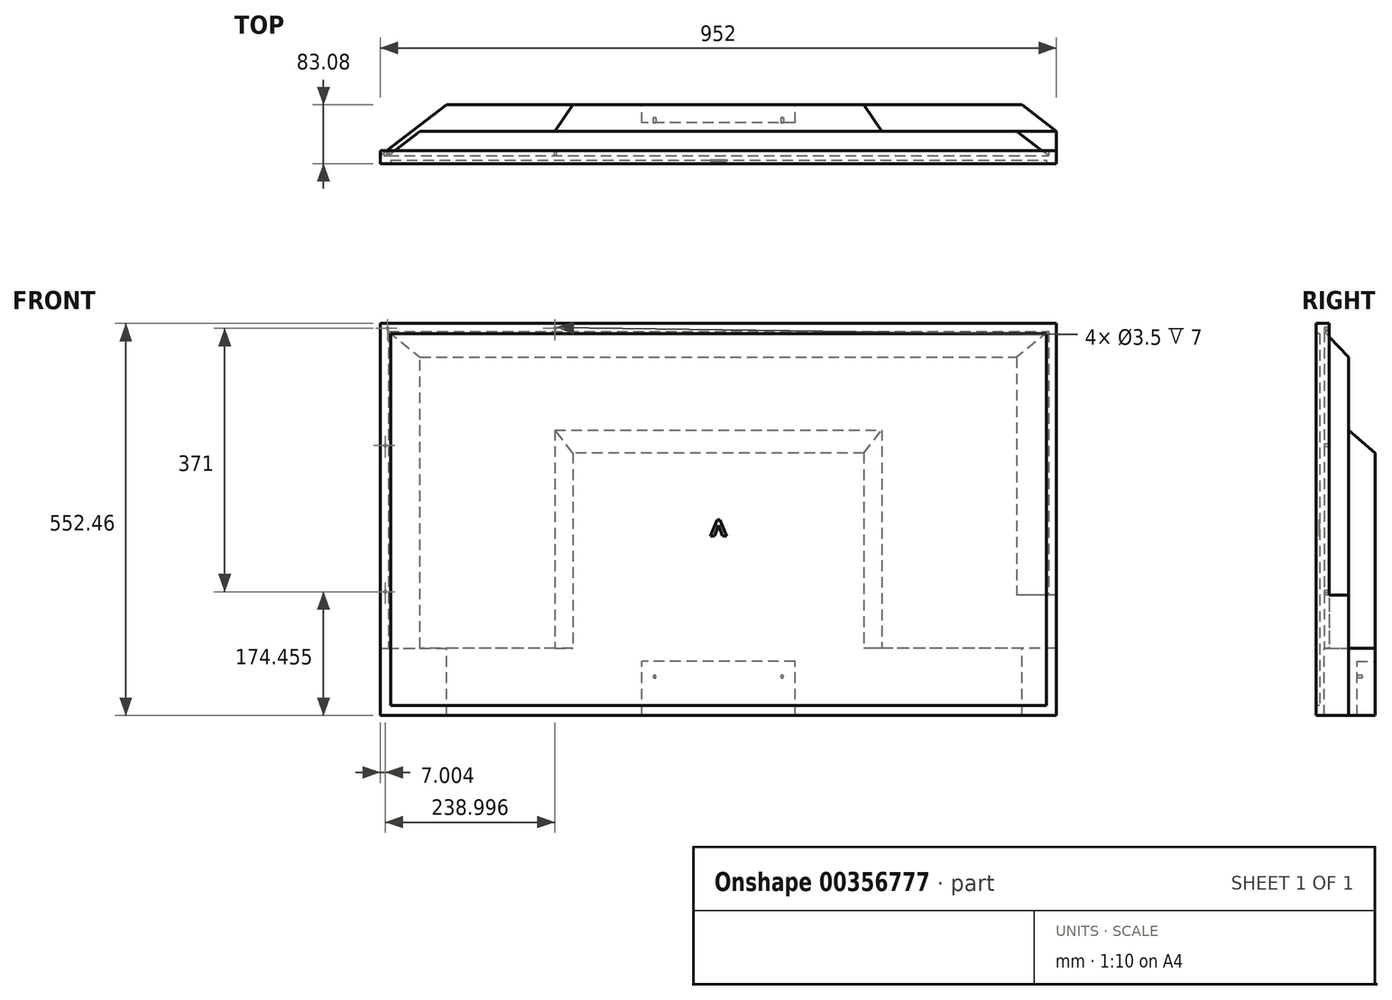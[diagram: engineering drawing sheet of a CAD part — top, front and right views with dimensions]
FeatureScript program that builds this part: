
annotation { "Feature Type Name" : "Feature", "Feature Type Description" : "" }
export const myFeature = defineFeature(function(context is Context, id is Id, definition is map)
    precondition{}
    {
        {
            var Q0;
            Q0=qCreatedBy(makeId("Front.planeOp"),FACE);
            var sketch = newSketch(context, id + "F0", { "sketchPlane" : qUnion([Q0])});
            skLineSegment(sketch, "E0.bottom", {"start": v(476, 276.23) * mm, "end": v(-476, 276.23) * mm});
            skLineSegment(sketch, "E0.top", {"start": v(476, -276.23) * mm, "end": v(-476, -276.23) * mm});
            skLineSegment(sketch, "E0.left", {"start": v(476, 276.23) * mm, "end": v(476, -276.23) * mm});
            skLineSegment(sketch, "E0.right", {"start": v(-476, 276.23) * mm, "end": v(-476, -276.23) * mm});
            skPoint(sketch, "E0.middle", {"position": v(0, 0) * mm});
            skSolve(sketch);
        }
        {
            var Q0;
            Q0 = qSketchRegion(id + "F0", true);
            extrude(context, id + "F1", {"entities" : qUnion([Q0]), "oppositeDirection" : true, "depth" : 11.7 * mm});
        }
        {
            var Q0;
            Q0=makeQuery(id+"F1.opExtrude","CAP_FACE",FACE,{"disambiguationData":[OSD([sQuery(id+"F0.wireOp",EDGE,"E0.bottom"),sQuery(id+"F0.wireOp",EDGE,"E0.top"),sQuery(id+"F0.wireOp",EDGE,"E0.left"),sQuery(id+"F0.wireOp",EDGE,"E0.right")])],"isStart":true});
            var sketch = newSketch(context, id + "F2", { "sketchPlane" : qUnion([Q0])});
            skLineSegment(sketch, "E1.bottom", {"start": v(-476, 276.23) * mm, "end": v(476, 276.23) * mm});
            skLineSegment(sketch, "E1.top", {"start": v(-476, -276.23) * mm, "end": v(476, -276.23) * mm});
            skLineSegment(sketch, "E1.left", {"start": v(-476, 276.23) * mm, "end": v(-476, -276.23) * mm});
            skLineSegment(sketch, "E1.right", {"start": v(476, 276.23) * mm, "end": v(476, -276.23) * mm});
            skLineSegment(sketch, "E2.0", {"start": v(-461.7, 261.93) * mm, "end": v(461.7, 261.93) * mm});
            skLineSegment(sketch, "E2.1", {"start": v(-461.7, 261.93) * mm, "end": v(-461.7, -261.93) * mm});
            skLineSegment(sketch, "E2.2", {"start": v(-461.7, -261.93) * mm, "end": v(461.7, -261.93) * mm});
            skLineSegment(sketch, "E2.3", {"start": v(461.7, 261.93) * mm, "end": v(461.7, -261.93) * mm});
            skSolve(sketch);
        }
        {
            var Q0;
            Q0=makeQuery(id+"F2.imprint","IMPRINT",FACE,{"disambiguationData":[TD([[makeQuery(id+"F2.imprint","IMPRINT",EDGE,{"derivedFrom":sQuery(id+"F2.wireOp",EDGE,"E2.0")}),-1.0]])]});
            extrude(context, id + "F3", {"entities" : qUnion([Q0]), "operationType" : NewBodyOperationType.REMOVE, "oppositeDirection" : true, "depth" : 5 * mm});
        }
        {
            var Q0;
            Q0=makeQuery(id+"F3.boolean.opBoolean","COPY",FACE,{"derivedFrom":makeQuery(id+"F3.opExtrude","CAP_FACE",FACE,{"disambiguationData":[OSD([sQuery(id+"F2.wireOp",EDGE,"E2.0"),sQuery(id+"F2.wireOp",EDGE,"E2.1"),sQuery(id+"F2.wireOp",EDGE,"E2.2"),sQuery(id+"F2.wireOp",EDGE,"E2.3")])],"isStart":false})});
            var sketch = newSketch(context, id + "F4", { "sketchPlane" : qUnion([Q0])});
            skText(sketch, "E3", { "text": "^", "fontName": "RobotoSlab-Regular.ttf"});
            const initialGuessF4  = {"E3": [-0.01344, -0.04589, 1, 0, 0.04588]};
            skSetInitialGuess(sketch, initialGuessF4);
            skSolve(sketch);
        }
        {
            var Q0;
            Q0 = qSketchRegion(id + "F4", true);
            extrude(context, id + "F5", {"entities" : qUnion([Q0]), "operationType" : NewBodyOperationType.ADD, "depth" : 1 * mm});
        }
        {
            var Q0;
            Q0=makeQuery(id+"F1.opExtrude","CAP_FACE",FACE,{"disambiguationData":[OSD([sQuery(id+"F0.wireOp",EDGE,"E0.bottom"),sQuery(id+"F0.wireOp",EDGE,"E0.top"),sQuery(id+"F0.wireOp",EDGE,"E0.left"),sQuery(id+"F0.wireOp",EDGE,"E0.right")])],"isStart":false});
            var sketch = newSketch(context, id + "F6", { "sketchPlane" : qUnion([Q0])});
            skLineSegment(sketch, "E4.bottom", {"start": v(464.8, 265.03) * mm, "end": v(-464.8, 265.03) * mm});
            skLineSegment(sketch, "E4.top", {"start": v(464.8, -265.03) * mm, "end": v(-464.8, -265.03) * mm});
            skLineSegment(sketch, "E4.left", {"start": v(464.8, 265.03) * mm, "end": v(464.8, -265.03) * mm});
            skLineSegment(sketch, "E4.right", {"start": v(-464.8, 265.03) * mm, "end": v(-464.8, -265.03) * mm});
            skPoint(sketch, "E4.middle", {"position": v(0, 0) * mm});
            skLineSegment(sketch, "E5.top", {"start": v(-476, -106.23) * mm, "end": v(0, -106.23) * mm});
            skLineSegment(sketch, "E5.left", {"start": v(-476, -276.23) * mm, "end": v(-476, -106.23) * mm});
            skLineSegment(sketch, "E5.right", {"start": v(0, -276.23) * mm, "end": v(0, -106.23) * mm});
            skLineSegment(sketch, "E6.top", {"start": v(476, -181.22) * mm, "end": v(0, -181.22) * mm});
            skLineSegment(sketch, "E6.left", {"start": v(476, -276.23) * mm, "end": v(476, -181.22) * mm});
            skSolve(sketch);
        }
        {
            var Q0;
            Q0 = qSketchRegion(id + "F6", true);
            var Q1;
            {var subQ0=sQuery(id+"F6.wireOp",EDGE,"E5.left");Q1=makeQuery(id+"F6.imprint","IMPRINT",FACE,{"disambiguationData":[TD([[makeQuery(id+"F6.imprint","IMPRINT",EDGE,{"derivedFrom":subQ0}),1.0]])]});}
            var Q2;
            {var subQ0=sQuery(id+"F6.wireOp",EDGE,"E6.left");Q2=makeQuery(id+"F6.imprint","IMPRINT",FACE,{"disambiguationData":[TD([[makeQuery(id+"F6.imprint","IMPRINT",EDGE,{"derivedFrom":subQ0}),-1.0]])]});}
            extrude(context, id + "F7", {"entities" : qUnion([Q0, Q1, Q2]), "operationType" : NewBodyOperationType.ADD, "depth" : 34.34 * mm});
        }
        {
            var Q0;
            Q0=makeQuery(id+"F7.opExtrude","SWEPT_FACE",FACE,{"disambiguationData":[OSD([sQuery(id+"F6.wireOp",EDGE,"E4.bottom")])]});
            var sketch = newSketch(context, id + "F8", { "sketchPlane" : qUnion([Q0])});
            skLineSegment(sketch, "E7", {"start": v(-464.8, 11.7) * mm, "end": v(-420.03, 46.04) * mm});
            skLineSegment(sketch, "E8", {"start": v(-420.03, 46.04) * mm, "end": v(-464.8, 46.04) * mm});
            skLineSegment(sketch, "E9", {"start": v(-464.8, 46.04) * mm, "end": v(-464.8, 11.7) * mm});
            skSolve(sketch);
        }
        {
            var Q0;
            Q0=makeQuery(id+"F8.imprint","IMPRINT",FACE,{"disambiguationData":[TD([[makeQuery(id+"F8.imprint","IMPRINT",EDGE,{"derivedFrom":sQuery(id+"F8.wireOp",EDGE,"E7")}),1.0]])]});
            var Q1;
            Q1=makeQuery(id+"F7.opExtrude","SWEPT_FACE",FACE,{"disambiguationData":[OSD([sQuery(id+"F6.wireOp",EDGE,"E6.top")])]});
            extrude(context, id + "F9", {"entities" : qUnion([Q0]), "operationType" : NewBodyOperationType.REMOVE, "endBound" : BoundingType.UP_TO_SURFACE, "oppositeDirection" : true, "endBoundEntityFace" : qUnion([Q1]), "depth" : 400 * mm});
        }
        {
            var Q0;
            Q0=makeQuery(id+"F7.opExtrude","SWEPT_FACE",FACE,{"disambiguationData":[OSD([sQuery(id+"F6.wireOp",EDGE,"E4.right")])]});
            var sketch = newSketch(context, id + "F10", { "sketchPlane" : qUnion([Q0])});
            skLineSegment(sketch, "E10", {"start": v(11.7, 265.03) * mm, "end": v(46.04, 228.6) * mm});
            skLineSegment(sketch, "E11", {"start": v(46.04, 228.6) * mm, "end": v(46.04, 265.03) * mm});
            skLineSegment(sketch, "E12", {"start": v(46.04, 265.03) * mm, "end": v(11.7, 265.03) * mm});
            skSolve(sketch);
        }
        {
            var Q0;
            Q0=makeQuery(id+"F10.imprint","IMPRINT",FACE,{"disambiguationData":[TD([[makeQuery(id+"F10.imprint","IMPRINT",EDGE,{"derivedFrom":sQuery(id+"F10.wireOp",EDGE,"E10")}),1.0]])]});
            var Q1;
            Q1=makeQuery(id+"F7.boolean.opBoolean","MERGE",FACE,{"derivedFrom":[makeQuery(id+"F1.opExtrude","SWEPT_FACE",FACE,{"disambiguationData":[OSD([sQuery(id+"F0.wireOp",EDGE,"E0.right")])]}),makeQuery(id+"F7.opExtrude","SWEPT_FACE",FACE,{"disambiguationData":[OSD([sQuery(id+"F6.wireOp",EDGE,"E6.left")])]})]});
            extrude(context, id + "F11", {"entities" : qUnion([Q0]), "operationType" : NewBodyOperationType.REMOVE, "endBound" : BoundingType.UP_TO_SURFACE, "oppositeDirection" : true, "endBoundEntityFace" : qUnion([Q1]), "depth" : 25 * mm});
        }
        {
            var Q0;
            Q0=makeQuery(id+"F7.opExtrude","SWEPT_FACE",FACE,{"disambiguationData":[OSD([sQuery(id+"F6.wireOp",EDGE,"E5.top")])]});
            var sketch = newSketch(context, id + "F12", { "sketchPlane" : qUnion([Q0])});
            skLineSegment(sketch, "E13", {"start": v(464.8, 11.7) * mm, "end": v(420.03, 46.04) * mm});
            skLineSegment(sketch, "E14", {"start": v(420.03, 46.04) * mm, "end": v(464.8, 46.04) * mm});
            skLineSegment(sketch, "E15", {"start": v(464.8, 46.04) * mm, "end": v(464.8, 11.7) * mm});
            skSolve(sketch);
        }
        {
            var Q0;
            Q0 = qSketchRegion(id + "F12", true);
            var Q1;
            Q1=makeQuery(id+"F1.opExtrude","SWEPT_FACE",FACE,{"disambiguationData":[OSD([sQuery(id+"F0.wireOp",EDGE,"E0.bottom")])]});
            extrude(context, id + "F13", {"entities" : qUnion([Q0]), "operationType" : NewBodyOperationType.REMOVE, "endBound" : BoundingType.UP_TO_SURFACE, "endBoundEntityFace" : qUnion([Q1]), "depth" : 25 * mm});
        }
        {
            var Q0;
            Q0=makeQuery(id+"F7.opExtrude","CAP_FACE",FACE,{"disambiguationData":[OSD([sQuery(id+"F0.wireOp",EDGE,"E0.top"),sQuery(id+"F6.wireOp",EDGE,"E4.bottom"),sQuery(id+"F6.wireOp",EDGE,"E4.left"),sQuery(id+"F6.wireOp",EDGE,"E4.right"),sQuery(id+"F6.wireOp",EDGE,"E5.top"),sQuery(id+"F6.wireOp",EDGE,"E5.left"),sQuery(id+"F6.wireOp",EDGE,"E6.top"),sQuery(id+"F6.wireOp",EDGE,"E6.left")])],"isStart":false});
            var sketch = newSketch(context, id + "F14", { "sketchPlane" : qUnion([Q0])});
            skLineSegment(sketch, "E16.bottom", {"start": v(230, 126.23) * mm, "end": v(-230, 126.23) * mm});
            skLineSegment(sketch, "E16.top", {"start": v(230, -126.23) * mm, "end": v(-230, -126.23) * mm});
            skLineSegment(sketch, "E16.left", {"start": v(230, 126.23) * mm, "end": v(230, -126.23) * mm});
            skLineSegment(sketch, "E16.right", {"start": v(-230, 126.23) * mm, "end": v(-230, -126.23) * mm});
            skPoint(sketch, "E16.middle", {"position": v(0, 0) * mm});
            skLineSegment(sketch, "E17.bottom", {"start": v(-476, -276.23) * mm, "end": v(476, -276.23) * mm});
            skLineSegment(sketch, "E17.top", {"start": v(-476, -181.22) * mm, "end": v(476, -181.22) * mm});
            skLineSegment(sketch, "E17.left", {"start": v(-476, -276.23) * mm, "end": v(-476, -181.22) * mm});
            skLineSegment(sketch, "E17.right", {"start": v(476, -276.23) * mm, "end": v(476, -181.22) * mm});
            skLineSegment(sketch, "E18", {"start": v(-230, -126.23) * mm, "end": v(-230, -181.22) * mm});
            skLineSegment(sketch, "E19", {"start": v(230, -126.23) * mm, "end": v(230, -181.22) * mm});
            skSolve(sketch);
        }
        {
            var Q0;
            Q0 = qSketchRegion(id + "F14", true);
            extrude(context, id + "F15", {"entities" : qUnion([Q0]), "operationType" : NewBodyOperationType.ADD, "depth" : 37.05 * mm});
        }
        {
            var Q0;
            {var subQ0=sQuery(id+"F14.wireOp",EDGE,"E17.top");var subQ2=sQuery(id+"F6.wireOp",EDGE,"E6.top");Q0=makeQuery(id+"F15.boolean.opBoolean","MERGE",FACE,{"derivedFrom":[makeQuery(id+"F9.boolean.opBoolean","MERGE",FACE,{"derivedFrom":[makeQuery(id+"F7.opExtrude","SWEPT_FACE",FACE,{"disambiguationData":[OSD([subQ2])]}),makeQuery(id+"F9.opExtrude","CAP_FACE",FACE,{"disambiguationData":[OSD([subQ2])],"isStart":false})]}),makeQuery(id+"F15.opExtrude","SWEPT_FACE",FACE,{"disambiguationData":[OSD([subQ0]),TDD([makeQuery(id+"F14.imprint","IMPRINT",EDGE,{"disambiguationData":[TD([[makeQuery(id+"F14.imprint","INTERSECT",VERTEX,{"derivedFrom":[subQ0,sQuery(id+"F14.wireOp",EDGE,"E17.right")]}),-1.0]])],"derivedFrom":subQ0}),makeQuery(id+"F14.imprint","IMPRINT",EDGE,{"disambiguationData":[TD([[makeQuery(id+"F14.imprint","INTERSECT",VERTEX,{"derivedFrom":[subQ0,sQuery(id+"F14.wireOp",EDGE,"E19")]}),-1.0]])],"derivedFrom":subQ0})])]})]});}
            var sketch = newSketch(context, id + "F16", { "sketchPlane" : qUnion([Q0])});
            skLineSegment(sketch, "E20", {"start": v(-476, 11.7) * mm, "end": v(-384.43, 81.94) * mm});
            skLineSegment(sketch, "E21", {"start": v(-384.43, 81.94) * mm, "end": v(-382.93, 83.08) * mm});
            skLineSegment(sketch, "E22", {"start": v(-382.93, 83.08) * mm, "end": v(-476, 83.08) * mm});
            skLineSegment(sketch, "E23", {"start": v(-476, 83.08) * mm, "end": v(-476, 11.7) * mm});
            skSolve(sketch);
        }
        {
            var Q0;
            Q0=makeQuery(id+"F16.imprint","IMPRINT",FACE,{"disambiguationData":[TD([[makeQuery(id+"F16.imprint","IMPRINT",EDGE,{"derivedFrom":sQuery(id+"F16.wireOp",EDGE,"E20")}),1.0]])]});
            var Q1;
            {var subQ0=sQuery(id+"F0.wireOp",EDGE,"E0.top");Q1=makeQuery(id+"F15.boolean.opBoolean","MERGE",FACE,{"derivedFrom":[makeQuery(id+"F7.boolean.opBoolean","MERGE",FACE,{"derivedFrom":[makeQuery(id+"F1.opExtrude","SWEPT_FACE",FACE,{"disambiguationData":[OSD([subQ0])]}),makeQuery(id+"F7.opExtrude","SWEPT_FACE",FACE,{"disambiguationData":[OSD([subQ0])]})]}),makeQuery(id+"F15.opExtrude","SWEPT_FACE",FACE,{"disambiguationData":[OSD([sQuery(id+"F14.wireOp",EDGE,"E17.bottom")])]})]});}
            extrude(context, id + "F17", {"entities" : qUnion([Q0]), "operationType" : NewBodyOperationType.REMOVE, "endBound" : BoundingType.UP_TO_SURFACE, "oppositeDirection" : true, "endBoundEntityFace" : qUnion([Q1]), "depth" : 25 * mm});
        }
        {
            var Q0;
            Q0=makeQuery(id+"F15.opExtrude","SWEPT_FACE",FACE,{"disambiguationData":[OSD([sQuery(id+"F14.wireOp",EDGE,"E16.left"),sQuery(id+"F14.wireOp",EDGE,"E19")])]});
            var sketch = newSketch(context, id + "F18", { "sketchPlane" : qUnion([Q0])});
            skLineSegment(sketch, "E24", {"start": v(-46.04, 126.23) * mm, "end": v(-83.08, 93.77) * mm});
            skLineSegment(sketch, "E25", {"start": v(-83.08, 93.77) * mm, "end": v(-83.08, 126.23) * mm});
            skLineSegment(sketch, "E26", {"start": v(-83.08, 126.23) * mm, "end": v(-46.04, 126.23) * mm});
            skSolve(sketch);
        }
        {
            var Q0;
            Q0=makeQuery(id+"F18.imprint","IMPRINT",FACE,{"disambiguationData":[TD([[makeQuery(id+"F18.imprint","IMPRINT",EDGE,{"derivedFrom":sQuery(id+"F18.wireOp",EDGE,"E24")}),-1.0]])]});
            var Q1;
            Q1=makeQuery(id+"F15.opExtrude","SWEPT_FACE",FACE,{"disambiguationData":[OSD([sQuery(id+"F14.wireOp",EDGE,"E16.right"),sQuery(id+"F14.wireOp",EDGE,"E18")])]});
            extrude(context, id + "F19", {"entities" : qUnion([Q0]), "operationType" : NewBodyOperationType.REMOVE, "endBound" : BoundingType.UP_TO_SURFACE, "oppositeDirection" : true, "endBoundEntityFace" : qUnion([Q1]), "depth" : 25 * mm});
        }
        {
            var Q0;
            {var subQ0=sQuery(id+"F14.wireOp",EDGE,"E17.top");var subQ2=sQuery(id+"F6.wireOp",EDGE,"E6.top");Q0=makeQuery(id+"F15.boolean.opBoolean","MERGE",FACE,{"derivedFrom":[makeQuery(id+"F9.boolean.opBoolean","MERGE",FACE,{"derivedFrom":[makeQuery(id+"F7.opExtrude","SWEPT_FACE",FACE,{"disambiguationData":[OSD([subQ2])]}),makeQuery(id+"F9.opExtrude","CAP_FACE",FACE,{"disambiguationData":[OSD([subQ2])],"isStart":false})]}),makeQuery(id+"F15.opExtrude","SWEPT_FACE",FACE,{"disambiguationData":[OSD([subQ0]),TDD([makeQuery(id+"F14.imprint","IMPRINT",EDGE,{"disambiguationData":[TD([[makeQuery(id+"F14.imprint","INTERSECT",VERTEX,{"derivedFrom":[subQ0,sQuery(id+"F14.wireOp",EDGE,"E17.right")]}),-1.0]])],"derivedFrom":subQ0}),makeQuery(id+"F14.imprint","IMPRINT",EDGE,{"disambiguationData":[TD([[makeQuery(id+"F14.imprint","INTERSECT",VERTEX,{"derivedFrom":[subQ0,sQuery(id+"F14.wireOp",EDGE,"E19")]}),-1.0]])],"derivedFrom":subQ0})])]})]});}
            var sketch = newSketch(context, id + "F20", { "sketchPlane" : qUnion([Q0])});
            skLineSegment(sketch, "E27", {"start": v(-230, 46.04) * mm, "end": v(-205, 83.08) * mm});
            skLineSegment(sketch, "E28", {"start": v(-205, 83.08) * mm, "end": v(-230, 83.08) * mm});
            skLineSegment(sketch, "E29", {"start": v(-230, 83.08) * mm, "end": v(-230, 46.04) * mm});
            skLineSegment(sketch, "E30.MirrorCS", {"start": v(205, 83.08) * mm, "end": v(230, 83.08) * mm});
            skLineSegment(sketch, "E31.MirrorCS", {"start": v(230, 83.08) * mm, "end": v(230, 46.04) * mm});
            skLineSegment(sketch, "E32.MirrorCS", {"start": v(230, 46.04) * mm, "end": v(205, 83.08) * mm});
            skSolve(sketch);
        }
        {
            var Q0;
            Q0 = qSketchRegion(id + "F20", true);
            var Q1;
            Q1=makeQuery(id+"F1.opExtrude","SWEPT_FACE",FACE,{"disambiguationData":[OSD([sQuery(id+"F0.wireOp",EDGE,"E0.bottom")])]});
            extrude(context, id + "F21", {"entities" : qUnion([Q0]), "operationType" : NewBodyOperationType.REMOVE, "endBound" : BoundingType.UP_TO_SURFACE, "endBoundEntityFace" : qUnion([Q1]), "depth" : 25 * mm});
        }
        {
            var Q0;
            {var subQ0=sQuery(id+"F14.wireOp",EDGE,"E17.top");Q0=makeQuery(id+"F21.boolean.opBoolean","MERGE",FACE,{"derivedFrom":[makeQuery(id+"F15.opExtrude","SWEPT_FACE",FACE,{"disambiguationData":[OSD([subQ0]),TDD([makeQuery(id+"F14.imprint","IMPRINT",EDGE,{"disambiguationData":[TD([[makeQuery(id+"F14.imprint","INTERSECT",VERTEX,{"derivedFrom":[subQ0,sQuery(id+"F14.wireOp",EDGE,"E18")]}),1.0]])],"derivedFrom":subQ0})])]}),makeQuery(id+"F21.opExtrude","CAP_FACE",FACE,{"disambiguationData":[OSD([sQuery(id+"F20.wireOp",EDGE,"E30.MirrorCS"),sQuery(id+"F20.wireOp",EDGE,"E31.MirrorCS"),sQuery(id+"F20.wireOp",EDGE,"E32.MirrorCS")])],"isStart":true})]});}
            var sketch = newSketch(context, id + "F22", { "sketchPlane" : qUnion([Q0])});
            skLineSegment(sketch, "E33", {"start": v(476, 46.04) * mm, "end": v(427.7, 83.08) * mm});
            skLineSegment(sketch, "E34", {"start": v(427.7, 83.08) * mm, "end": v(476, 83.08) * mm});
            skLineSegment(sketch, "E35", {"start": v(476, 83.08) * mm, "end": v(476, 46.04) * mm});
            skSolve(sketch);
        }
        {
            var Q0;
            Q0 = qSketchRegion(id + "F22", true);
            var Q1;
            {var subQ0=sQuery(id+"F0.wireOp",EDGE,"E0.top");Q1=makeQuery(id+"F15.boolean.opBoolean","MERGE",FACE,{"derivedFrom":[makeQuery(id+"F7.boolean.opBoolean","MERGE",FACE,{"derivedFrom":[makeQuery(id+"F1.opExtrude","SWEPT_FACE",FACE,{"disambiguationData":[OSD([subQ0])]}),makeQuery(id+"F7.opExtrude","SWEPT_FACE",FACE,{"disambiguationData":[OSD([subQ0])]})]}),makeQuery(id+"F15.opExtrude","SWEPT_FACE",FACE,{"disambiguationData":[OSD([sQuery(id+"F14.wireOp",EDGE,"E17.bottom")])]})]});}
            extrude(context, id + "F23", {"entities" : qUnion([Q0]), "operationType" : NewBodyOperationType.REMOVE, "endBound" : BoundingType.UP_TO_SURFACE, "oppositeDirection" : true, "endBoundEntityFace" : qUnion([Q1]), "depth" : 25 * mm});
        }
        {
            var Q0;
            Q0=makeQuery(id+"F1.opExtrude","CAP_FACE",FACE,{"disambiguationData":[OSD([sQuery(id+"F0.wireOp",EDGE,"E0.bottom"),sQuery(id+"F0.wireOp",EDGE,"E0.top"),sQuery(id+"F0.wireOp",EDGE,"E0.left"),sQuery(id+"F0.wireOp",EDGE,"E0.right")])],"isStart":false});
            var sketch = newSketch(context, id + "F24", { "sketchPlane" : qUnion([Q0])});
            skCircle(sketch, "E36", {"center": v(-465.65, 269.23) * mm, "radius": 1.75 * mm});
            skCircle(sketch, "E37", {"center": v(-469, 104.23) * mm, "radius": 1.75 * mm});
            skCircle(sketch, "E38", {"center": v(-469, -101.77) * mm, "radius": 1.75 * mm});
            skCircle(sketch, "E39", {"center": v(-230, 269.23) * mm, "radius": 1.75 * mm});
            skCircle(sketch, "E40", {"center": v(0, 269.23) * mm, "radius": 1.75 * mm});
            skCircle(sketch, "E41.MirrorC", {"center": v(469, -101.77) * mm, "radius": 1.75 * mm});
            skCircle(sketch, "E42.MirrorC", {"center": v(469, 104.23) * mm, "radius": 1.75 * mm});
            skCircle(sketch, "E43.MirrorC", {"center": v(465.65, 269.23) * mm, "radius": 1.75 * mm});
            skCircle(sketch, "E44.MirrorC", {"center": v(230, 269.23) * mm, "radius": 1.75 * mm});
            skSolve(sketch);
        }
        {
            var Q0;
            Q0=makeQuery(id+"F24.imprint","IMPRINT",FACE,{"disambiguationData":[TD([[makeQuery(id+"F24.imprint","IMPRINT",EDGE,{"derivedFrom":sQuery(id+"F24.wireOp",EDGE,"E36")}),1.0]])]});
            var Q1;
            Q1=makeQuery(id+"F24.imprint","IMPRINT",FACE,{"disambiguationData":[TD([[makeQuery(id+"F24.imprint","IMPRINT",EDGE,{"derivedFrom":sQuery(id+"F24.wireOp",EDGE,"E37")}),1.0]])]});
            var Q2;
            Q2=makeQuery(id+"F24.imprint","IMPRINT",FACE,{"disambiguationData":[TD([[makeQuery(id+"F24.imprint","IMPRINT",EDGE,{"derivedFrom":sQuery(id+"F24.wireOp",EDGE,"E38")}),1.0]])]});
            var Q3;
            Q3=makeQuery(id+"F24.imprint","IMPRINT",FACE,{"disambiguationData":[TD([[makeQuery(id+"F24.imprint","IMPRINT",EDGE,{"derivedFrom":sQuery(id+"F24.wireOp",EDGE,"E39")}),1.0]])]});
            var Q4;
            Q4=makeQuery(id+"F24.imprint","IMPRINT",FACE,{"disambiguationData":[TD([[makeQuery(id+"F24.imprint","IMPRINT",EDGE,{"derivedFrom":sQuery(id+"F24.wireOp",EDGE,"E40")}),1.0]])]});
            var Q5;
            Q5=makeQuery(id+"F24.imprint","IMPRINT",FACE,{"disambiguationData":[TD([[makeQuery(id+"F24.imprint","IMPRINT",EDGE,{"derivedFrom":sQuery(id+"F24.wireOp",EDGE,"E44.MirrorC")}),-1.0]])]});
            var Q6;
            Q6=makeQuery(id+"F24.imprint","IMPRINT",FACE,{"disambiguationData":[TD([[makeQuery(id+"F24.imprint","IMPRINT",EDGE,{"derivedFrom":sQuery(id+"F24.wireOp",EDGE,"E43.MirrorC")}),-1.0]])]});
            var Q7;
            Q7=makeQuery(id+"F24.imprint","IMPRINT",FACE,{"disambiguationData":[TD([[makeQuery(id+"F24.imprint","IMPRINT",EDGE,{"derivedFrom":sQuery(id+"F24.wireOp",EDGE,"E42.MirrorC")}),-1.0]])]});
            var Q8;
            Q8=makeQuery(id+"F24.imprint","IMPRINT",FACE,{"disambiguationData":[TD([[makeQuery(id+"F24.imprint","IMPRINT",EDGE,{"derivedFrom":sQuery(id+"F24.wireOp",EDGE,"E41.MirrorC")}),-1.0]])]});
            extrude(context, id + "F25", {"entities" : qUnion([Q0, Q1, Q2, Q3, Q4, Q5, Q6, Q7, Q8]), "operationType" : NewBodyOperationType.ADD, "depth" : 7 * mm});
        }
        {
            var Q0;
            Q0=makeQuery(id+"F15.opExtrude","CAP_FACE",FACE,{"disambiguationData":[OSD([sQuery(id+"F14.wireOp",EDGE,"E16.bottom"),sQuery(id+"F14.wireOp",EDGE,"E16.left"),sQuery(id+"F14.wireOp",EDGE,"E16.right"),sQuery(id+"F14.wireOp",EDGE,"E17.bottom"),sQuery(id+"F14.wireOp",EDGE,"E17.top"),sQuery(id+"F14.wireOp",EDGE,"E17.left"),sQuery(id+"F14.wireOp",EDGE,"E17.right"),sQuery(id+"F14.wireOp",EDGE,"E18"),sQuery(id+"F14.wireOp",EDGE,"E19")])],"isStart":false});
            var sketch = newSketch(context, id + "F26", { "sketchPlane" : qUnion([Q0])});
            skLineSegment(sketch, "E45.bottom", {"start": v(-107.95, -276.23) * mm, "end": v(107.95, -276.23) * mm});
            skLineSegment(sketch, "E45.top", {"start": v(-107.95, -200.03) * mm, "end": v(107.95, -200.03) * mm});
            skLineSegment(sketch, "E45.left", {"start": v(-107.95, -276.23) * mm, "end": v(-107.95, -200.03) * mm});
            skLineSegment(sketch, "E45.right", {"start": v(107.95, -276.23) * mm, "end": v(107.95, -200.03) * mm});
            skSolve(sketch);
        }
        {
            var Q0;
            Q0 = qSketchRegion(id + "F26", true);
            extrude(context, id + "F27", {"entities" : qUnion([Q0]), "operationType" : NewBodyOperationType.REMOVE, "oppositeDirection" : true, "depth" : 25.4 * mm});
        }
        {
            var Q0;
            Q0=makeQuery(id+"F27.boolean.opBoolean","COPY",FACE,{"derivedFrom":makeQuery(id+"F27.opExtrude","CAP_FACE",FACE,{"disambiguationData":[OSD([sQuery(id+"F26.wireOp",EDGE,"E45.bottom"),sQuery(id+"F26.wireOp",EDGE,"E45.top"),sQuery(id+"F26.wireOp",EDGE,"E45.left"),sQuery(id+"F26.wireOp",EDGE,"E45.right")])],"isStart":false})});
            var sketch = newSketch(context, id + "F28", { "sketchPlane" : qUnion([Q0])});
            skCircle(sketch, "E46", {"center": v(-89.7, -221.23) * mm, "radius": 1.92 * mm});
            skCircle(sketch, "E47.MirrorC", {"center": v(89.7, -221.23) * mm, "radius": 1.92 * mm});
            skSolve(sketch);
        }
        {
            var Q0;
            Q0 = qSketchRegion(id + "F28", true);
            extrude(context, id + "F29", {"entities" : qUnion([Q0]), "operationType" : NewBodyOperationType.ADD, "depth" : 7 * mm});
        }
    });
